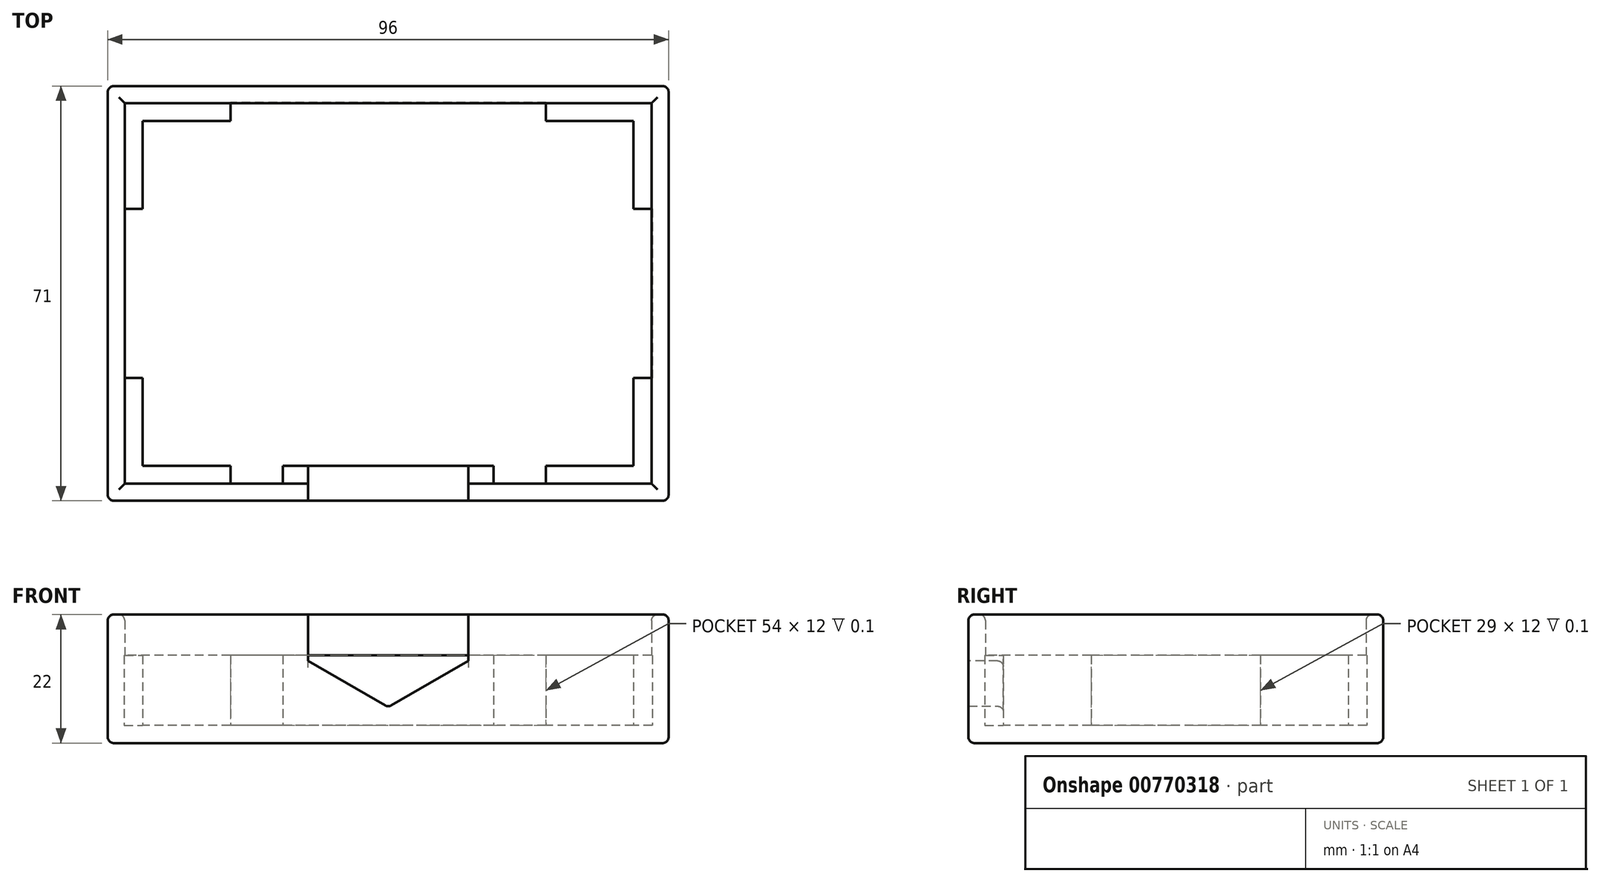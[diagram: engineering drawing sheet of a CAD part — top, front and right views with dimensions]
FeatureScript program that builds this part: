
annotation { "Feature Type Name" : "Feature", "Feature Type Description" : "" }
export const myFeature = defineFeature(function(context is Context, id is Id, definition is map)
    precondition{}
    {
        {
            var Q0;
            Q0=qCreatedBy(makeId("Top.planeOp"),FACE);
            var sketch = newSketch(context, id + "F0", { "sketchPlane" : qUnion([Q0])});
            skLineSegment(sketch, "E0.bottom", {"start": v(45.1, 32.6) * mm, "end": v(-45.1, 32.6) * mm});
            skLineSegment(sketch, "E0.top", {"start": v(45.1, -32.6) * mm, "end": v(-45.1, -32.6) * mm});
            skLineSegment(sketch, "E0.left", {"start": v(45.1, 32.6) * mm, "end": v(45.1, -32.6) * mm});
            skLineSegment(sketch, "E0.right", {"start": v(-45.1, 32.6) * mm, "end": v(-45.1, -32.6) * mm});
            skPoint(sketch, "E0.middle", {"position": v(0, 0) * mm});
            skLineSegment(sketch, "E1.bottom", {"start": v(42, 29.5) * mm, "end": v(-42, 29.5) * mm});
            skLineSegment(sketch, "E1.top", {"start": v(42, -29.5) * mm, "end": v(-42, -29.5) * mm});
            skLineSegment(sketch, "E1.left", {"start": v(42, 29.5) * mm, "end": v(42, -29.5) * mm});
            skLineSegment(sketch, "E1.right", {"start": v(-42, 29.5) * mm, "end": v(-42, -29.5) * mm});
            skLineSegment(sketch, "E2.bottom", {"start": v(48, 35.5) * mm, "end": v(-48, 35.5) * mm});
            skLineSegment(sketch, "E2.top", {"start": v(48, -35.5) * mm, "end": v(-48, -35.5) * mm});
            skLineSegment(sketch, "E2.left", {"start": v(48, 35.5) * mm, "end": v(48, -35.5) * mm});
            skLineSegment(sketch, "E2.right", {"start": v(-48, 35.5) * mm, "end": v(-48, -35.5) * mm});
            skSolve(sketch);
        }
        {
            var Q0;
            Q0=makeQuery(id+"F0.imprint","IMPRINT",FACE,{"disambiguationData":[TD([[makeQuery(id+"F0.imprint","IMPRINT",EDGE,{"derivedFrom":sQuery(id+"F0.wireOp",EDGE,"E1.bottom")}),1.0]])]});
            extrude(context, id + "F1", {"entities" : qUnion([Q0]), "depth" : 3 * mm, "offsetDistance" : 25 * mm});
        }
        {
            var Q0;
            Q0=makeQuery(id+"F0.imprint","IMPRINT",FACE,{"disambiguationData":[TD([[makeQuery(id+"F0.imprint","IMPRINT",EDGE,{"derivedFrom":sQuery(id+"F0.wireOp",EDGE,"E0.bottom")}),1.0]])]});
            extrude(context, id + "F2", {"entities" : qUnion([Q0]), "operationType" : NewBodyOperationType.ADD, "depth" : 15 * mm, "offsetDistance" : 25 * mm});
        }
        {
            var Q0;
            Q0=makeQuery(id+"F0.imprint","IMPRINT",FACE,{"disambiguationData":[TD([[makeQuery(id+"F0.imprint","IMPRINT",EDGE,{"derivedFrom":sQuery(id+"F0.wireOp",EDGE,"E0.bottom")}),-1.0]])]});
            extrude(context, id + "F3", {"entities" : qUnion([Q0]), "operationType" : NewBodyOperationType.ADD, "depth" : 22 * mm, "offsetDistance" : 25 * mm});
        }
        {
            var Q0;
            Q0=makeQuery(id+"F3.opExtrude","SWEPT_FACE",FACE,{"disambiguationData":[OSD([sQuery(id+"F0.wireOp",EDGE,"E2.top")])]});
            var sketch = newSketch(context, id + "F4", { "sketchPlane" : qUnion([Q0])});
            skCircle(sketch, "E3.cCircle", {"center": v(0, 22) * mm, "radius": 13.73 * mm, "construction": true});
            skLineSegment(sketch, "E3.0", {"start": v(13.73, 29.93) * mm, "end": v(13.73, 14.07) * mm});
            skLineSegment(sketch, "E3.1", {"start": v(13.73, 14.07) * mm, "end": v(0, 6.15) * mm});
            skLineSegment(sketch, "E3.2", {"start": v(0, 6.15) * mm, "end": v(-13.73, 14.07) * mm});
            skLineSegment(sketch, "E3.3", {"start": v(-13.73, 14.07) * mm, "end": v(-13.73, 29.93) * mm});
            skLineSegment(sketch, "E3.4", {"start": v(-13.73, 29.93) * mm, "end": v(0, 37.85) * mm});
            skLineSegment(sketch, "E3.5", {"start": v(0, 37.85) * mm, "end": v(13.73, 29.93) * mm});
            skPoint(sketch, "E3.0.midPoint", {"position": v(13.73, 22) * mm});
            skSolve(sketch);
        }
        {
            var Q0;
            {var subQ4=sQuery(id+"F4.wireOp",EDGE,"E3.1");Q0=makeQuery(id+"F4.imprint","IMPRINT",FACE,{"disambiguationData":[TD([[makeQuery(id+"F4.imprint","IMPRINT",EDGE,{"derivedFrom":subQ4}),-1.0]])]});}
            extrude(context, id + "F5", {"entities" : qUnion([Q0]), "operationType" : NewBodyOperationType.REMOVE, "oppositeDirection" : true, "depth" : 6.5 * mm, "offsetDistance" : 25 * mm});
        }
        {
            var Q0;
            Q0=makeQuery(id+"F2.opExtrude","SWEPT_FACE",FACE,{"disambiguationData":[OSD([sQuery(id+"F0.wireOp",EDGE,"E1.right")])]});
            var sketch = newSketch(context, id + "F6", { "sketchPlane" : qUnion([Q0])});
            skLineSegment(sketch, "E4", {"start": v(-29.5, 15) * mm, "end": v(-14.5, 15) * mm, "construction": true});
            skLineSegment(sketch, "E5", {"start": v(-14.5, 15) * mm, "end": v(-14.5, 3) * mm});
            skLineSegment(sketch, "E6.MirrorCS", {"start": v(14.5, 15) * mm, "end": v(14.5, 3) * mm});
            skSolve(sketch);
        }
        {
            var Q0;
            {var subQ0=sQuery(id+"F6.wireOp",EDGE,"E5");Q0=makeQuery(id+"F6.imprint","IMPRINT",FACE,{"disambiguationData":[TD([[makeQuery(id+"F6.imprint","IMPRINT",EDGE,{"derivedFrom":subQ0}),1.0]])]});}
            extrude(context, id + "F7", {"entities" : qUnion([Q0]), "operationType" : NewBodyOperationType.REMOVE, "oppositeDirection" : true, "depth" : 3.2 * mm, "offsetDistance" : 25 * mm});
        }
        {
            var Q0;
            Q0=makeQuery(id+"F2.opExtrude","SWEPT_FACE",FACE,{"disambiguationData":[OSD([sQuery(id+"F0.wireOp",EDGE,"E1.left")])]});
            var sketch = newSketch(context, id + "F8", { "sketchPlane" : qUnion([Q0])});
            skLineSegment(sketch, "E7", {"start": v(-29.5, 15) * mm, "end": v(-14.5, 15) * mm, "construction": true});
            skLineSegment(sketch, "E8", {"start": v(-14.5, 15) * mm, "end": v(-14.5, 3) * mm});
            skLineSegment(sketch, "E9.MirrorCS", {"start": v(14.5, 15) * mm, "end": v(14.5, 3) * mm});
            skSolve(sketch);
        }
        {
            var Q0;
            {var subQ0=sQuery(id+"F8.wireOp",EDGE,"E8");Q0=makeQuery(id+"F8.imprint","IMPRINT",FACE,{"disambiguationData":[TD([[makeQuery(id+"F8.imprint","IMPRINT",EDGE,{"derivedFrom":subQ0}),1.0]])]});}
            extrude(context, id + "F9", {"entities" : qUnion([Q0]), "operationType" : NewBodyOperationType.REMOVE, "oppositeDirection" : true, "depth" : 3.2 * mm, "offsetDistance" : 25 * mm});
        }
        {
            var Q0;
            Q0=makeQuery(id+"F2.opExtrude","SWEPT_FACE",FACE,{"disambiguationData":[OSD([sQuery(id+"F0.wireOp",EDGE,"E1.top")])]});
            var sketch = newSketch(context, id + "F10", { "sketchPlane" : qUnion([Q0])});
            skLineSegment(sketch, "E10", {"start": v(-42, 15) * mm, "end": v(-27, 15) * mm, "construction": true});
            skLineSegment(sketch, "E11", {"start": v(-27, 15) * mm, "end": v(-27, 3) * mm});
            skLineSegment(sketch, "E12.MirrorCS", {"start": v(27, 15) * mm, "end": v(27, 3) * mm});
            skLineSegment(sketch, "E13", {"start": v(-18.05, 15) * mm, "end": v(-18.05, 3) * mm});
            skLineSegment(sketch, "E14.MirrorCS", {"start": v(18.05, 15) * mm, "end": v(18.05, 3) * mm});
            skSolve(sketch);
        }
        {
            var Q0;
            {var subQ0=sQuery(id+"F10.wireOp",EDGE,"E11");Q0=makeQuery(id+"F10.imprint","IMPRINT",FACE,{"disambiguationData":[TD([[makeQuery(id+"F10.imprint","IMPRINT",EDGE,{"derivedFrom":subQ0}),1.0]])]});}
            var Q1;
            {var subQ0=sQuery(id+"F10.wireOp",EDGE,"E12.MirrorCS");Q1=makeQuery(id+"F10.imprint","IMPRINT",FACE,{"disambiguationData":[TD([[makeQuery(id+"F10.imprint","IMPRINT",EDGE,{"derivedFrom":subQ0}),-1.0]])]});}
            extrude(context, id + "F11", {"entities" : qUnion([Q0, Q1]), "operationType" : NewBodyOperationType.REMOVE, "oppositeDirection" : true, "depth" : 3.2 * mm, "offsetDistance" : 25 * mm});
        }
        {
            var Q0;
            Q0=makeQuery(id+"F2.opExtrude","SWEPT_FACE",FACE,{"disambiguationData":[OSD([sQuery(id+"F0.wireOp",EDGE,"E1.bottom")])]});
            var sketch = newSketch(context, id + "F12", { "sketchPlane" : qUnion([Q0])});
            skLineSegment(sketch, "E15", {"start": v(-42, 15) * mm, "end": v(-27, 15) * mm, "construction": true});
            skLineSegment(sketch, "E16", {"start": v(-27, 15) * mm, "end": v(-27, 3) * mm});
            skLineSegment(sketch, "E17.MirrorCS", {"start": v(27, 15) * mm, "end": v(27, 3) * mm});
            skSolve(sketch);
        }
        {
            var Q0;
            {var subQ0=sQuery(id+"F12.wireOp",EDGE,"E16");Q0=makeQuery(id+"F12.imprint","IMPRINT",FACE,{"disambiguationData":[TD([[makeQuery(id+"F12.imprint","IMPRINT",EDGE,{"derivedFrom":subQ0}),1.0]])]});}
            extrude(context, id + "F13", {"entities" : qUnion([Q0]), "operationType" : NewBodyOperationType.REMOVE, "oppositeDirection" : true, "depth" : 3.2 * mm, "offsetDistance" : 25 * mm});
        }
        {
            var Q0;
            {var subQ0=sQuery(id+"F0.wireOp",EDGE,"E2.right");var subQ1=sQuery(id+"F0.wireOp",EDGE,"E2.top");Q0=makeQuery(id+"F5.boolean.opBoolean","SPLIT",EDGE,{"disambiguationData":[TD([makeQuery(id+"F3.opExtrude","SWEPT_FACE",FACE,{"disambiguationData":[OSD([subQ0])]})])],"derivedFrom":makeQuery(id+"F3.opExtrude","CAP_EDGE",EDGE,{"disambiguationData":[OSD([subQ1])],"isStart":false})});}
            var Q1;
            Q1=makeQuery(id+"F3.opExtrude","CAP_EDGE",EDGE,{"disambiguationData":[OSD([sQuery(id+"F0.wireOp",EDGE,"E2.right")])],"isStart":false});
            var Q2;
            Q2=makeQuery(id+"F3.opExtrude","SWEPT_EDGE",EDGE,{"disambiguationData":[OSD([sQuery(id+"F0.wireOp",EDGE,"E2.top"),sQuery(id+"F0.wireOp",EDGE,"E2.right")])]});
            var Q3;
            Q3=makeQuery(id+"F3.opExtrude","SWEPT_EDGE",EDGE,{"disambiguationData":[OSD([sQuery(id+"F0.wireOp",EDGE,"E2.top"),sQuery(id+"F0.wireOp",EDGE,"E2.left")])]});
            var Q4;
            Q4=makeQuery(id+"F3.opExtrude","CAP_EDGE",EDGE,{"disambiguationData":[OSD([sQuery(id+"F0.wireOp",EDGE,"E2.left")])],"isStart":true});
            var Q5;
            Q5=makeQuery(id+"F3.opExtrude","CAP_EDGE",EDGE,{"disambiguationData":[OSD([sQuery(id+"F0.wireOp",EDGE,"E2.top")])],"isStart":true});
            var Q6;
            {var subQ0=sQuery(id+"F0.wireOp",EDGE,"E2.left");var subQ1=sQuery(id+"F0.wireOp",EDGE,"E2.top");Q6=makeQuery(id+"F5.boolean.opBoolean","SPLIT",EDGE,{"disambiguationData":[TD([makeQuery(id+"F3.opExtrude","SWEPT_FACE",FACE,{"disambiguationData":[OSD([subQ0])]})])],"derivedFrom":makeQuery(id+"F3.opExtrude","CAP_EDGE",EDGE,{"disambiguationData":[OSD([subQ1])],"isStart":false})});}
            var Q7;
            Q7=makeQuery(id+"F5.boolean.opBoolean","COPY",EDGE,{"derivedFrom":makeQuery(id+"F5.opExtrude","CAP_EDGE",EDGE,{"disambiguationData":[OSD([sQuery(id+"F4.wireOp",EDGE,"E3.1")])],"isStart":true})});
            var Q8;
            Q8=makeQuery(id+"F5.boolean.opBoolean","COPY",EDGE,{"derivedFrom":makeQuery(id+"F5.opExtrude","CAP_EDGE",EDGE,{"disambiguationData":[OSD([sQuery(id+"F4.wireOp",EDGE,"E3.2")])],"isStart":true})});
            var Q9;
            Q9=makeQuery(id+"F5.boolean.opBoolean","COPY",EDGE,{"derivedFrom":makeQuery(id+"F5.opExtrude","CAP_EDGE",EDGE,{"disambiguationData":[OSD([sQuery(id+"F4.wireOp",EDGE,"E3.3")])],"isStart":true})});
            var Q10;
            Q10=makeQuery(id+"F5.boolean.opBoolean","COPY",EDGE,{"derivedFrom":makeQuery(id+"F5.opExtrude","CAP_EDGE",EDGE,{"disambiguationData":[OSD([sQuery(id+"F4.wireOp",EDGE,"E3.0")])],"isStart":true})});
            var Q11;
            Q11=makeQuery(id+"F3.opExtrude","CAP_EDGE",EDGE,{"disambiguationData":[OSD([sQuery(id+"F0.wireOp",EDGE,"E2.left")])],"isStart":false});
            var Q12;
            Q12=makeQuery(id+"F3.opExtrude","SWEPT_EDGE",EDGE,{"disambiguationData":[OSD([sQuery(id+"F0.wireOp",EDGE,"E2.bottom"),sQuery(id+"F0.wireOp",EDGE,"E2.left")])]});
            var Q13;
            Q13=makeQuery(id+"F3.opExtrude","CAP_EDGE",EDGE,{"disambiguationData":[OSD([sQuery(id+"F0.wireOp",EDGE,"E2.bottom")])],"isStart":false});
            var Q14;
            Q14=makeQuery(id+"F3.opExtrude","CAP_EDGE",EDGE,{"disambiguationData":[OSD([sQuery(id+"F0.wireOp",EDGE,"E2.bottom")])],"isStart":true});
            var Q15;
            Q15=makeQuery(id+"F3.opExtrude","SWEPT_EDGE",EDGE,{"disambiguationData":[OSD([sQuery(id+"F0.wireOp",EDGE,"E2.bottom"),sQuery(id+"F0.wireOp",EDGE,"E2.right")])]});
            var Q16;
            Q16=makeQuery(id+"F3.opExtrude","CAP_EDGE",EDGE,{"disambiguationData":[OSD([sQuery(id+"F0.wireOp",EDGE,"E2.right")])],"isStart":true});
            var Q17;
            Q17=makeQuery(id+"F3.opExtrude","CAP_EDGE",EDGE,{"disambiguationData":[OSD([sQuery(id+"F0.wireOp",EDGE,"E0.bottom")])],"isStart":false});
            var Q18;
            Q18=makeQuery(id+"F3.opExtrude","CAP_EDGE",EDGE,{"disambiguationData":[OSD([sQuery(id+"F0.wireOp",EDGE,"E0.right")])],"isStart":false});
            var Q19;
            Q19=makeQuery(id+"F3.opExtrude","CAP_EDGE",EDGE,{"disambiguationData":[OSD([sQuery(id+"F0.wireOp",EDGE,"E0.left")])],"isStart":false});
            var Q20;
            {var subQ0=sQuery(id+"F0.wireOp",EDGE,"E0.left");var subQ1=sQuery(id+"F0.wireOp",EDGE,"E0.top");Q20=makeQuery(id+"F5.boolean.opBoolean","SPLIT",EDGE,{"disambiguationData":[TD([makeQuery(id+"F3.opExtrude","SWEPT_FACE",FACE,{"disambiguationData":[OSD([subQ0])]})])],"derivedFrom":makeQuery(id+"F3.opExtrude","CAP_EDGE",EDGE,{"disambiguationData":[OSD([subQ1])],"isStart":false})});}
            var Q21;
            {var subQ0=sQuery(id+"F0.wireOp",EDGE,"E0.right");var subQ1=sQuery(id+"F0.wireOp",EDGE,"E0.top");Q21=makeQuery(id+"F5.boolean.opBoolean","SPLIT",EDGE,{"disambiguationData":[TD([makeQuery(id+"F3.opExtrude","SWEPT_FACE",FACE,{"disambiguationData":[OSD([subQ0])]})])],"derivedFrom":makeQuery(id+"F3.opExtrude","CAP_EDGE",EDGE,{"disambiguationData":[OSD([subQ1])],"isStart":false})});}
            var Q22;
            Q22=makeQuery(id+"F5.boolean.opBoolean","INTERSECT",EDGE,{"derivedFrom":[makeQuery(id+"F2.opExtrude","SWEPT_FACE",FACE,{"disambiguationData":[OSD([sQuery(id+"F0.wireOp",EDGE,"E1.top")])]}),makeQuery(id+"F5.opExtrude","SWEPT_FACE",FACE,{"disambiguationData":[OSD([sQuery(id+"F4.wireOp",EDGE,"E3.1")])]})]});
            var Q23;
            Q23=makeQuery(id+"F5.boolean.opBoolean","INTERSECT",EDGE,{"derivedFrom":[makeQuery(id+"F2.opExtrude","SWEPT_FACE",FACE,{"disambiguationData":[OSD([sQuery(id+"F0.wireOp",EDGE,"E1.top")])]}),makeQuery(id+"F5.opExtrude","SWEPT_FACE",FACE,{"disambiguationData":[OSD([sQuery(id+"F4.wireOp",EDGE,"E3.2")])]})]});
            var Q24;
            Q24=makeQuery(id+"F5.boolean.opBoolean","COPY",EDGE,{"derivedFrom":makeQuery(id+"F5.opExtrude","SWEPT_EDGE",EDGE,{"disambiguationData":[OSD([sQuery(id+"F4.wireOp",EDGE,"E3.1"),sQuery(id+"F4.wireOp",EDGE,"E3.2")])]})});
            fillet(context, id + "F14", {"entities" : qUnion([Q0, Q1, Q2, Q3, Q4, Q5, Q6, Q7, Q8, Q9, Q10, Q11, Q12, Q13, Q14, Q15, Q16, Q17, Q18, Q19, Q20, Q21, Q22, Q23, Q24]), "radius" : 1 * mm, "tangentPropagation" : true, "allowEdgeOverflow" : false});
        }
    });
